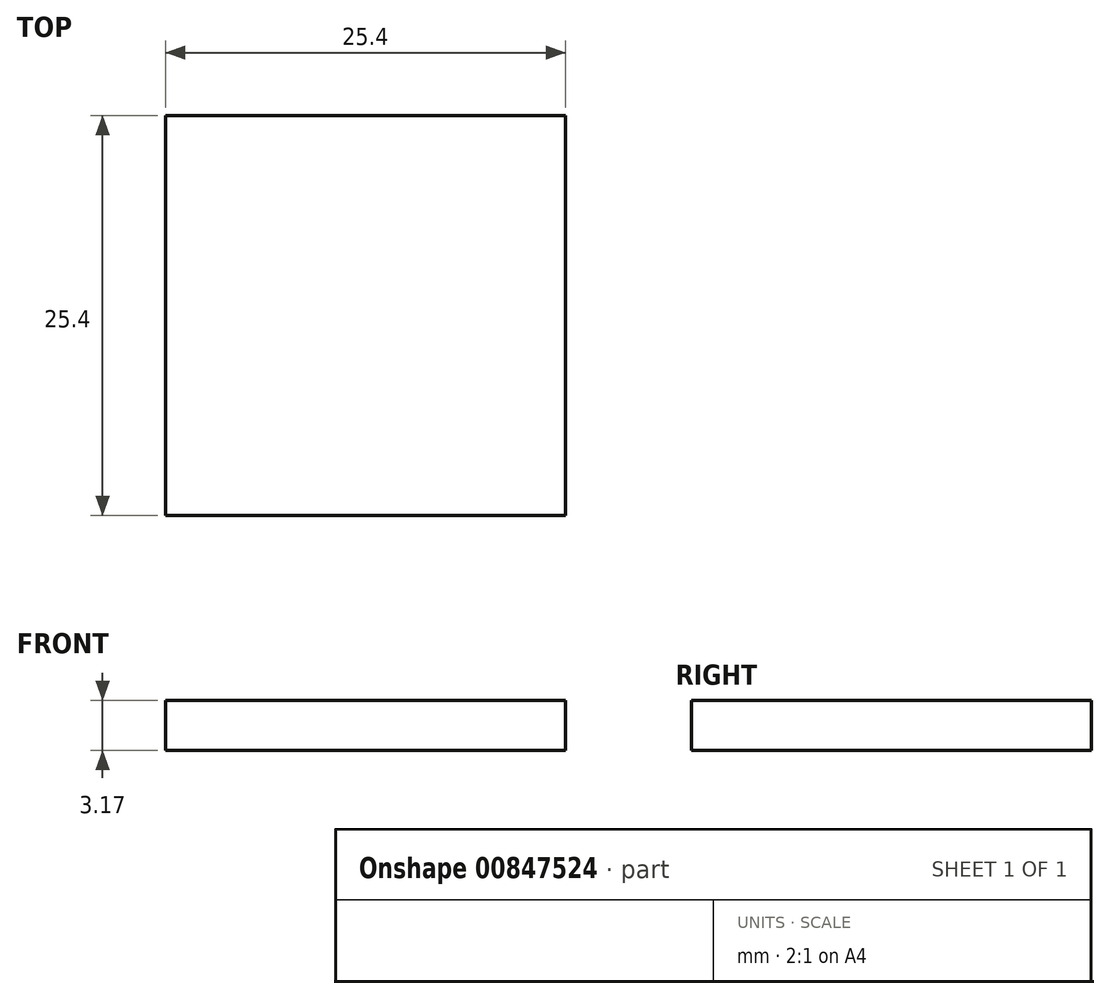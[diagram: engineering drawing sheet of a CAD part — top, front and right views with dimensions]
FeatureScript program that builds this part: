
annotation { "Feature Type Name" : "Feature", "Feature Type Description" : "" }
export const myFeature = defineFeature(function(context is Context, id is Id, definition is map)
    precondition{}
    {
        {
            var Q0;
            Q0=qCreatedBy(makeId("Top.planeOp"),FACE);
            var sketch = newSketch(context, id + "F0", { "sketchPlane" : qUnion([Q0])});
            skLineSegment(sketch, "E0.bottom", {"start": v(-9.73, 12.21) * mm, "end": v(15.67, 12.21) * mm});
            skLineSegment(sketch, "E0.top", {"start": v(-9.73, -13.19) * mm, "end": v(15.67, -13.19) * mm});
            skLineSegment(sketch, "E0.left", {"start": v(-9.73, 12.21) * mm, "end": v(-9.73, -13.19) * mm});
            skLineSegment(sketch, "E0.right", {"start": v(15.67, 12.21) * mm, "end": v(15.67, -13.19) * mm});
            skSolve(sketch);
        }
        {
            var Q0;
            Q0=makeQuery(id+"F0.imprint","IMPRINT",FACE,{"disambiguationData":[TD([[makeQuery(id+"F0.imprint","IMPRINT",EDGE,{"derivedFrom":sQuery(id+"F0.wireOp",EDGE,"E0.bottom")}),-1.0]])]});
            extrude(context, id + "F1", {"entities" : qUnion([Q0]), "depth" : 3.17 * mm, "offsetDistance" : 25.4 * mm});
        }
    });
